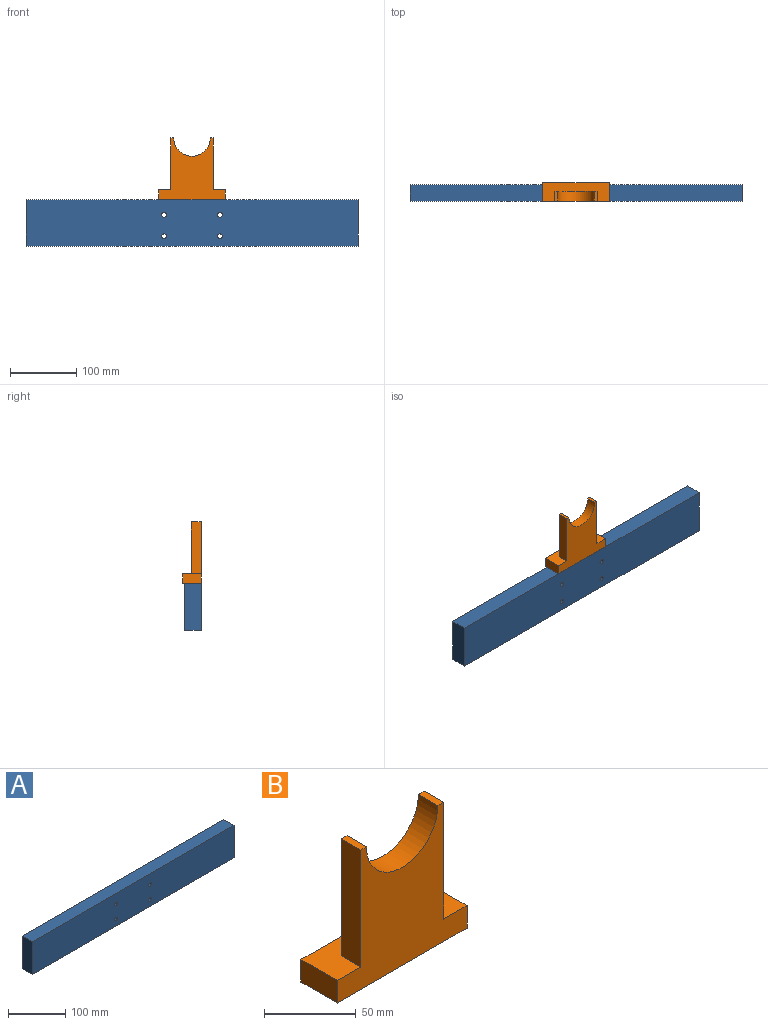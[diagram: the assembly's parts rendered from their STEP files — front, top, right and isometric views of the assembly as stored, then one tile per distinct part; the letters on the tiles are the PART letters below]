
ASSEMBLY  parts=2 mates=1
PART A: 10 faces, bbox 500x25x70 mm
  f0: plane 500x25mm, normal (0,0,-1), area 12500mm2, adj f1,f3,f4,f5
  f1: plane 500x70mm, normal (0,1,0), area 34846.1mm2, adj f0,f2,f4,f5,f6,f7,f8,f9
  f2: plane 500x25mm, normal (0,0,1), area 12500mm2, adj f1,f3,f4,f5
  f3: plane 500x70mm, normal (0,-1,0), area 34846.1mm2, adj f0,f2,f4,f5,f6,f7,f8,f9
  f4: plane 70x25mm, normal (1,0,0), area 1750mm2, adj f0,f1,f2,f3
  f5: plane 70x25mm, normal (-1,0,0), area 1750mm2, adj f0,f1,f2,f3
  f6: cylinder r=3.5mm len=25mm, axis (0,-1,0), area 549.8mm2, adj f1,f3
  f7: cylinder r=3.5mm len=25mm, axis (0,-1,0), area 549.8mm2, adj f1,f3
  f8: cylinder r=3.5mm len=25mm, axis (0,-1,0), area 549.8mm2, adj f1,f3
  f9: cylinder r=3.5mm len=25mm, axis (0,-1,0), area 549.8mm2, adj f1,f3
PART B: 12 faces, bbox 100x28x93 mm
  f0: plane 100x15mm, normal (0,1,0), area 1500mm2, adj f2,f3,f4,f5
  f1: plane 78x15mm, normal (-1,0,0), area 1170mm2, adj f5,f7,f8,f9
  f2: plane 28x15mm, normal (-1,0,0), area 420mm2, adj f0,f3,f5,f7
  f3: plane 100x28mm, normal (0,0,-1), area 2800mm2, adj f0,f2,f4,f7
  f4: plane 28x15mm, normal (1,0,0), area 420mm2, adj f0,f3,f5,f7
  f5: plane 100x28mm, normal (0,0,1), area 1840mm2, adj f0,f1,f2,f4,f6,f7,f8
  f6: plane 78x15mm, normal (1,0,0), area 1170mm2, adj f5,f7,f8,f11
  f7: plane 100x93mm, normal (0,-1,0), area 5304.1mm2, adj f1,f2,f3,f4,f5,f6,f9,f10
  f8: plane 78x64mm, normal (0,1,0), area 3804.1mm2, adj f1,f5,f6,f9,f10,f11
  f9: plane 15x4.5mm, normal (0,0,1), area 67.5mm2, adj f1,f7,f8,f10
  f10: cylinder r=27.5mm len=55mm, axis (0,-1,0), area 1295.9mm2, adj f7,f8,f9,f11
  f11: plane 15x4.5mm, normal (0,0,1), area 67.5mm2, adj f6,f7,f8,f10
PLACE A t=(3.17,0.49,-2.02)mm fixed
PLACE B t=(3.17,15.99,40.48)mm
MATE fastened B.f3 <-> A.f2  axis (0,0,-1) through (3.17,-12.01,32.98)mm
